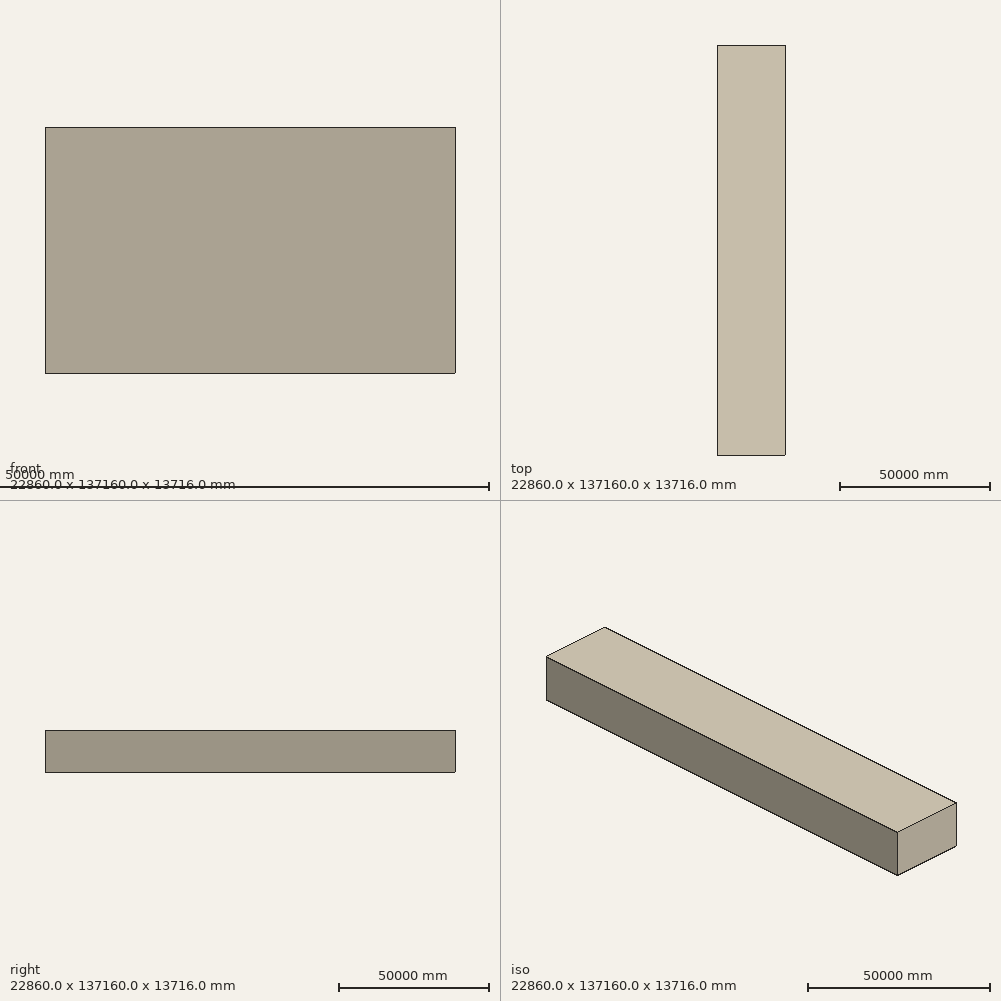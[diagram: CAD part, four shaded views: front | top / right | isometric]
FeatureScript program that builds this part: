
annotation { "Feature Type Name" : "Feature", "Feature Type Description" : "" }
export const myFeature = defineFeature(function(context is Context, id is Id, definition is map)
    precondition{}
    {
        {
            var Q0;
            Q0=qCreatedBy(makeId("Top.planeOp"),FACE);
            var sketch = newSketch(context, id + "F0", { "sketchPlane" : qUnion([Q0])});
            skLineSegment(sketch, "E0.bottom", {"start": v(-11430, 68580) * mm, "end": v(11430, 68580) * mm});
            skLineSegment(sketch, "E0.top", {"start": v(-11430, -68580) * mm, "end": v(11430, -68580) * mm});
            skLineSegment(sketch, "E0.left", {"start": v(-11430, 68580) * mm, "end": v(-11430, -68580) * mm});
            skLineSegment(sketch, "E0.right", {"start": v(11430, 68580) * mm, "end": v(11430, -68580) * mm});
            skLineSegment(sketch, "E1", {"start": v(-11430, 0) * mm, "end": v(11430, 0) * mm, "construction": true});
            skLineSegment(sketch, "E2", {"start": v(0, 68580) * mm, "end": v(0, -68580) * mm, "construction": true});
            skSolve(sketch);
        }
        {
            var Q0;
            Q0 = qSketchRegion(id + "F0", true);
            extrude(context, id + "F1", {"entities" : qUnion([Q0]), "depth" : 13716 * mm, "offsetDistance" : 25 * mm});
        }
    });
